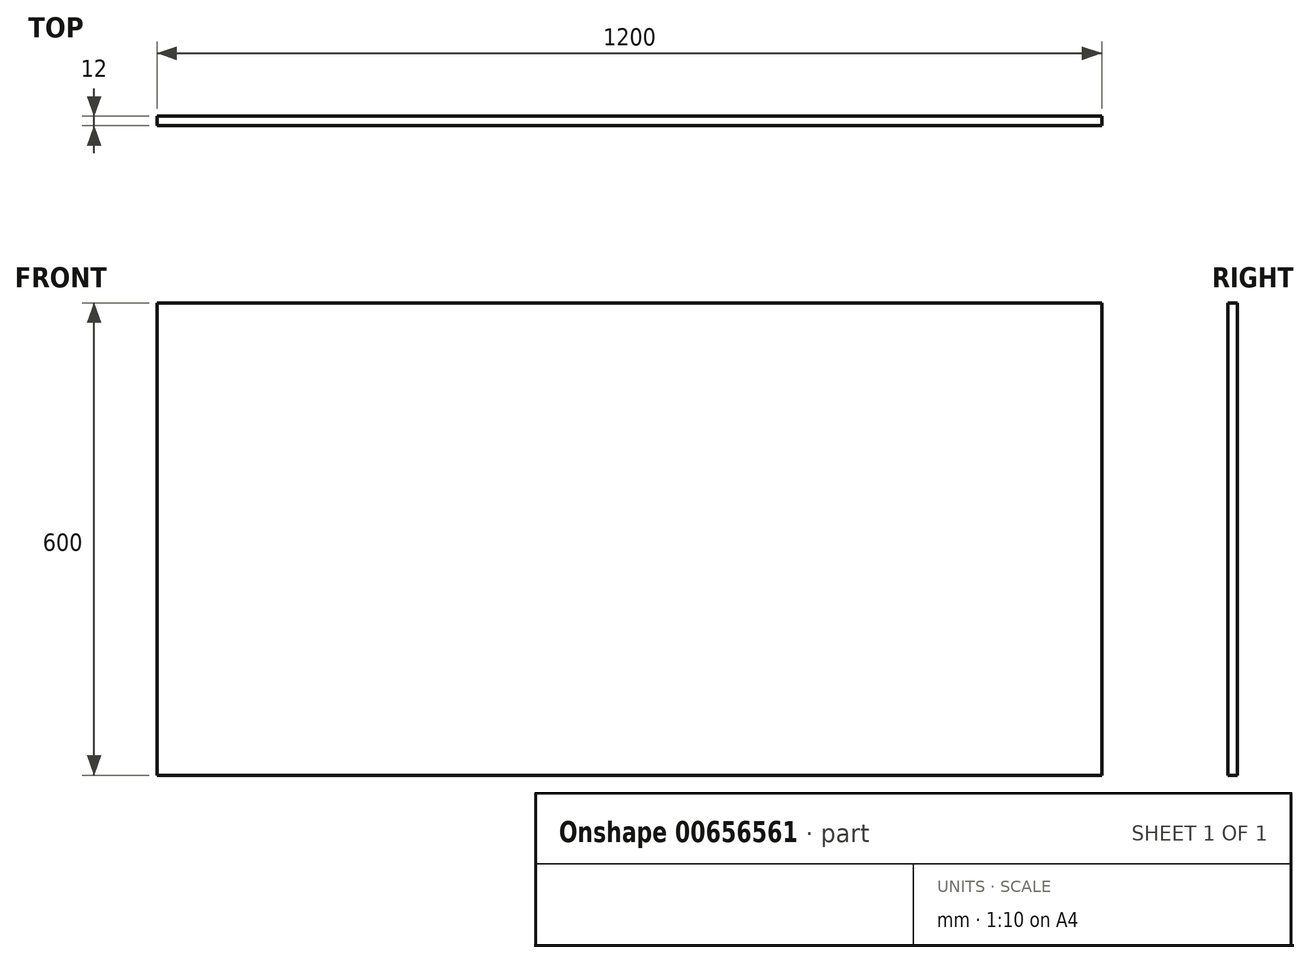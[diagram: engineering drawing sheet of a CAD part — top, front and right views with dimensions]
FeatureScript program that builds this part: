
annotation { "Feature Type Name" : "Feature", "Feature Type Description" : "" }
export const myFeature = defineFeature(function(context is Context, id is Id, definition is map)
    precondition{}
    {
        {
            var Q0;
            Q0=qCreatedBy(makeId("Front.planeOp"),FACE);
            var sketch = newSketch(context, id + "F0", { "sketchPlane" : qUnion([Q0])});
            skLineSegment(sketch, "E0.bottom", {"start": v(-543.4, 561.42) * mm, "end": v(656.6, 561.42) * mm});
            skLineSegment(sketch, "E0.top", {"start": v(-543.4, -38.58) * mm, "end": v(656.6, -38.58) * mm});
            skLineSegment(sketch, "E0.left", {"start": v(-543.4, 561.42) * mm, "end": v(-543.4, -38.58) * mm});
            skLineSegment(sketch, "E0.right", {"start": v(656.6, 561.42) * mm, "end": v(656.6, -38.58) * mm});
            skSolve(sketch);
        }
        {
            var Q0;
            Q0=makeQuery(id+"F0.imprint","IMPRINT",FACE,{"disambiguationData":[TD([[makeQuery(id+"F0.imprint","IMPRINT",EDGE,{"derivedFrom":sQuery(id+"F0.wireOp",EDGE,"E0.bottom")}),-1.0]])]});
            extrude(context, id + "F1", {"entities" : qUnion([Q0]), "depth" : 12 * mm, "offsetDistance" : 25 * mm});
        }
    });
